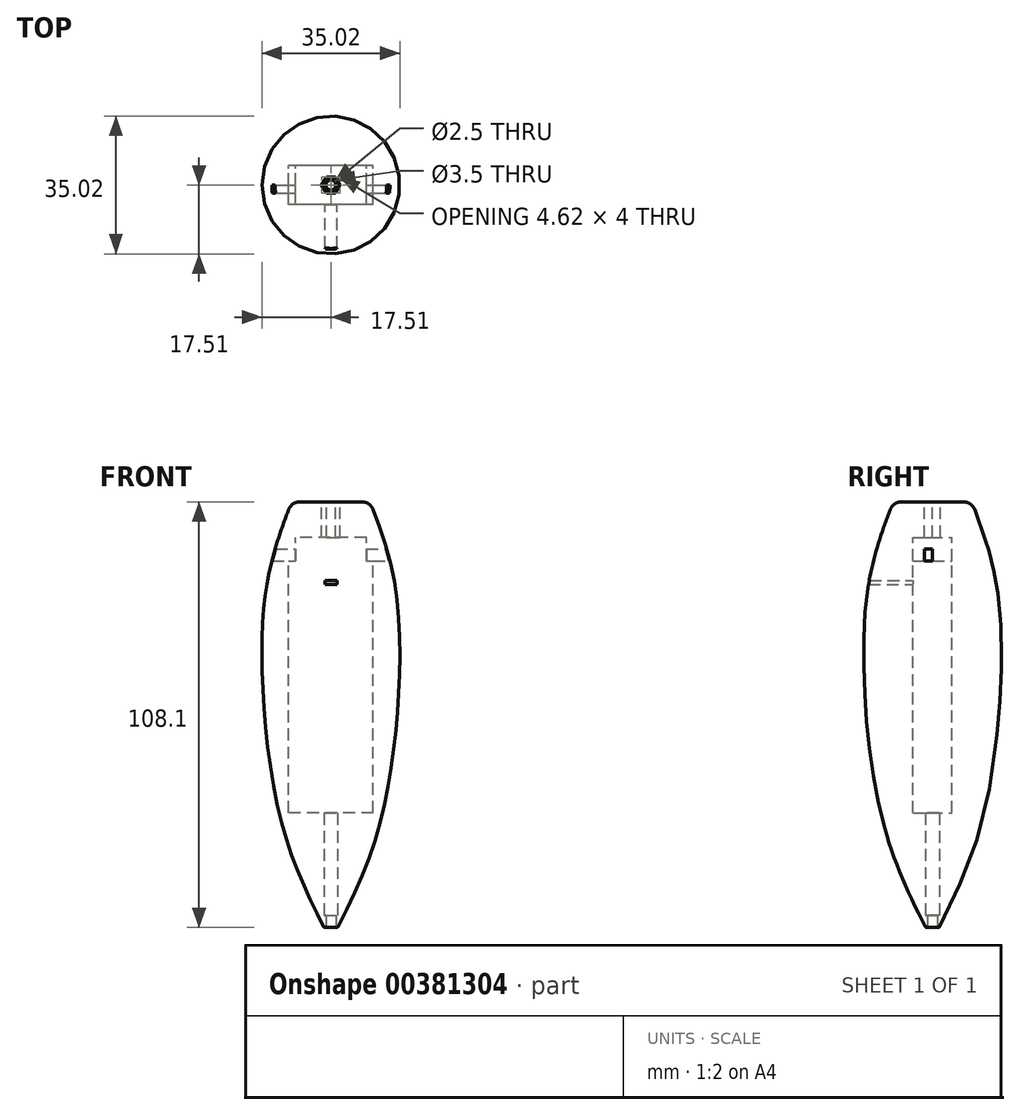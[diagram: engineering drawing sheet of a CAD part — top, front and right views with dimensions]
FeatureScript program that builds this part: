
annotation { "Feature Type Name" : "Feature", "Feature Type Description" : "" }
export const myFeature = defineFeature(function(context is Context, id is Id, definition is map)
    precondition{}
    {
        {
            var Q0;
            Q0=qCreatedBy(makeId("Front.planeOp"),FACE);
            var sketch = newSketch(context, id + "F0", { "sketchPlane" : qUnion([Q0])});
            skLineSegment(sketch, "E0.bottom", {"start": v(10.75, -17) * mm, "end": v(-10.75, -17) * mm});
            skLineSegment(sketch, "E0.top", {"start": v(10.75, 47) * mm, "end": v(9, 47) * mm});
            skLineSegment(sketch, "E0.left", {"start": v(10.75, -17) * mm, "end": v(10.75, 47) * mm});
            skLineSegment(sketch, "E0.right", {"start": v(-10.75, -17) * mm, "end": v(-10.75, 47) * mm});
            skPoint(sketch, "E0.middle", {"position": v(0, 15) * mm});
            skLineSegment(sketch, "E1", {"start": v(-10.75, 0) * mm, "end": v(10.75, 0) * mm, "construction": true});
            skLineSegment(sketch, "E2.top", {"start": v(9, 53) * mm, "end": v(-9, 53) * mm});
            skLineSegment(sketch, "E2.left", {"start": v(9, 47) * mm, "end": v(9, 53) * mm});
            skLineSegment(sketch, "E2.right", {"start": v(-9, 47) * mm, "end": v(-9, 53) * mm});
            skPoint(sketch, "E2.middle", {"position": v(0, 50) * mm});
            skPoint(sketch, "E2.middle.positionSnap0", {"position": v(0, 47) * mm});
            skPoint(sketch, "E2.centerSnap0", {"position": v(0, 47) * mm});
            skLineSegment(sketch, "E3.trimOffspring", {"start": v(-9, 47) * mm, "end": v(-10.75, 47) * mm});
            skSolve(sketch);
        }
        {
            var Q0;
            Q0=qCreatedBy(makeId("Front.planeOp"),FACE);
            var sketch = newSketch(context, id + "F1", { "sketchPlane" : qUnion([Q0])});
            skLineSegment(sketch, "E4", {"start": v(0, 0) * mm, "end": v(0, 25) * mm, "construction": true});
            skLineSegment(sketch, "E5", {"start": v(-17.5, 25) * mm, "end": v(17.5, 25) * mm, "construction": true});
            skLineSegment(sketch, "E6", {"start": v(-15, 47) * mm, "end": v(-2, 47) * mm, "construction": true});
            skPoint(sketch, "E7", {"position": v(0, 47) * mm});
            skPoint(sketch, "E8", {"position": v(0, -19.5) * mm});
            skLineSegment(sketch, "E9", {"start": v(-12.5, -19.5) * mm, "end": v(-1.25, -19.5) * mm, "construction": true});
            skLineSegment(sketch, "E10", {"start": v(0, -19.5) * mm, "end": v(0, -49.5) * mm, "construction": true});
            skLineSegment(sketch, "E11", {"start": v(0, 47) * mm, "end": v(0, 62) * mm, "construction": true});
            skLineSegment(sketch, "E12", {"start": v(-10, 62) * mm, "end": v(-2, 62) * mm});
            skFitSpline(sketch, "E13", {"points": [v(-10, 62) * mm, v(-15, 47) * mm, v(-17.5, 25) * mm, v(-12.5, -19.5) * mm, v(0, -49.5) * mm], "startDerivative": vector(-28.9, -76.62) * mm, "endDerivative": vector(51.56, -101.04) * mm});
            skLineSegment(sketch, "E14.0", {"start": v(-2, 50) * mm, "end": v(-2, 62) * mm});
            skPoint(sketch, "E15.orphan", {"position": v(10, 62) * mm});
            skLineSegment(sketch, "E16.0", {"start": v(-1.25, -43.05) * mm, "end": v(-1.25, -47.05) * mm});
            skLineSegment(sketch, "E17", {"start": v(0, 47) * mm, "end": v(-2, 47) * mm});
            skLineSegment(sketch, "E18", {"start": v(0, 50) * mm, "end": v(-2, 50) * mm});
            skLineSegment(sketch, "E19.trimOffspring", {"start": v(0, 47) * mm, "end": v(15, 47) * mm, "construction": true});
            skLineSegment(sketch, "E20.trimOffspring", {"start": v(0, -19.5) * mm, "end": v(12.5, -19.5) * mm, "construction": true});
            skLineSegment(sketch, "E21", {"start": v(0, 50) * mm, "end": v(0, -17) * mm});
            skLineSegment(sketch, "E22", {"start": v(0, -17) * mm, "end": v(-1.75, -17) * mm});
            skLineSegment(sketch, "E23", {"start": v(-1.75, -17) * mm, "end": v(-1.75, -43.05) * mm});
            skLineSegment(sketch, "E24", {"start": v(-1.25, -43.05) * mm, "end": v(-1.75, -43.05) * mm});
            skSolve(sketch);
        }
        {
            var Q0;
            Q0=makeQuery(id+"F1.imprint","IMPRINT",FACE,{"disambiguationData":[TD([[makeQuery(id+"F1.imprint","IMPRINT",EDGE,{"derivedFrom":sQuery(id+"F1.wireOp",EDGE,"E12")}),-1.0]])]});
            var Q1;
            Q1=sQuery(id+"F1.wireOp",EDGE,"E11");
            revolve(context, id + "F2", {"entities" : qUnion([Q0]), "axis" : qUnion([Q1]), "revolveType" : RevolveType.FULL});
        }
        {
            var Q0;
            Q0 = qSketchRegion(id + "F0", true);
            extrude(context, id + "F3", {"entities" : qUnion([Q0]), "operationType" : NewBodyOperationType.REMOVE, "endBound" : BoundingType.SYMMETRIC, "depth" : 10 * mm});
        }
        {
            var Q0;
            Q0=makeQuery(id+"F2.opRevolve","SWEPT_FACE",FACE,{"disambiguationData":[OSD([sQuery(id+"F1.wireOp",EDGE,"E12")])]});
            var sketch = newSketch(context, id + "F4", { "sketchPlane" : qUnion([Q0])});
            skCircle(sketch, "E25.cCircle", {"center": v(0, 0) * mm, "radius": 2 * mm, "construction": true});
            skLineSegment(sketch, "E25.0", {"start": v(2.3, 0) * mm, "end": v(1.15, -2) * mm});
            skLineSegment(sketch, "E25.1", {"start": v(1.15, -2) * mm, "end": v(-1.15, -2) * mm});
            skLineSegment(sketch, "E25.2", {"start": v(-1.15, -2) * mm, "end": v(-2.3, 0) * mm});
            skLineSegment(sketch, "E25.3", {"start": v(-2.3, 0) * mm, "end": v(-1.15, 2) * mm});
            skLineSegment(sketch, "E25.4", {"start": v(-1.15, 2) * mm, "end": v(1.15, 2) * mm});
            skLineSegment(sketch, "E25.5", {"start": v(1.15, 2) * mm, "end": v(2.3, 0) * mm});
            skPoint(sketch, "E25.0.midPoint", {"position": v(1.73, -1) * mm});
            skSolve(sketch);
        }
        {
            var Q0;
            Q0 = qSketchRegion(id + "F4", true);
            extrude(context, id + "F5", {"entities" : qUnion([Q0]), "operationType" : NewBodyOperationType.REMOVE, "oppositeDirection" : true, "depth" : 15 * mm});
        }
        {
            var Q0;
            Q0=qCreatedBy(makeId("Right.planeOp"),FACE);
            var sketch = newSketch(context, id + "F6", { "sketchPlane" : qUnion([Q0])});
            skLineSegment(sketch, "E26.bottom", {"start": v(0, 47) * mm, "end": v(-2, 47) * mm});
            skLineSegment(sketch, "E26.top", {"start": v(0, 50) * mm, "end": v(-2, 50) * mm});
            skLineSegment(sketch, "E26.left", {"start": v(0, 47) * mm, "end": v(0, 50) * mm});
            skLineSegment(sketch, "E26.right", {"start": v(-2, 47) * mm, "end": v(-2, 50) * mm});
            skPoint(sketch, "E26.middle", {"position": v(0, 48) * mm});
            skSolve(sketch);
        }
        {
            var Q0;
            Q0 = qSketchRegion(id + "F6", true);
            extrude(context, id + "F7", {"entities" : qUnion([Q0]), "operationType" : NewBodyOperationType.REMOVE, "endBound" : BoundingType.SYMMETRIC, "oppositeDirection" : true, "depth" : 41 * mm});
        }
        {
            var Q0;
            Q0=qCreatedBy(makeId("Front.planeOp"),FACE);
            var sketch = newSketch(context, id + "F8", { "sketchPlane" : qUnion([Q0])});
            skLineSegment(sketch, "E27.bottom", {"start": v(1.5, 41) * mm, "end": v(-1.5, 41) * mm});
            skLineSegment(sketch, "E27.top", {"start": v(1.5, 42) * mm, "end": v(-1.5, 42) * mm});
            skLineSegment(sketch, "E27.left", {"start": v(1.5, 41) * mm, "end": v(1.5, 42) * mm});
            skLineSegment(sketch, "E27.right", {"start": v(-1.5, 41) * mm, "end": v(-1.5, 42) * mm});
            skPoint(sketch, "E27.middle", {"position": v(0, 41.5) * mm});
            skSolve(sketch);
        }
        {
            var Q0;
            Q0 = qSketchRegion(id + "F8", true);
            extrude(context, id + "F9", {"entities" : qUnion([Q0]), "operationType" : NewBodyOperationType.REMOVE, "endBound" : BoundingType.THROUGH_ALL, "depth" : 25 * mm});
        }
        {
            var Q0;
            Q0=makeQuery(id+"F2.opRevolve","SWEPT_EDGE",EDGE,{"disambiguationData":[OSD([sQuery(id+"F1.wireOp",EDGE,"E13"),sQuery(id+"F1.wireOp",EDGE,"E16.0")])]});
            fillet(context, id + "F10", {"entities" : qUnion([Q0]), "radius" : 0.3 * mm, "tangentPropagation" : true, "allowEdgeOverflow" : false});
        }
        {
            var Q0;
            Q0=makeQuery(id+"F2.opRevolve","SWEPT_EDGE",EDGE,{"disambiguationData":[OSD([sQuery(id+"F1.wireOp",EDGE,"E16.0"),sQuery(id+"F1.wireOp",EDGE,"E24")])]});
            fillet(context, id + "F11", {"entities" : qUnion([Q0]), "radius" : 0.1 * mm, "tangentPropagation" : true, "allowEdgeOverflow" : false});
        }
        {
            var Q0;
            Q0=makeQuery(id+"F2.opRevolve","SWEPT_EDGE",EDGE,{"disambiguationData":[OSD([sQuery(id+"F1.wireOp",EDGE,"E23"),sQuery(id+"F1.wireOp",EDGE,"E24")])]});
            fillet(context, id + "F12", {"entities" : qUnion([Q0]), "radius" : 0.1 * mm, "tangentPropagation" : true, "allowEdgeOverflow" : false});
        }
        {
            var Q0;
            Q0=makeQuery(id+"F2.opRevolve","SWEPT_EDGE",EDGE,{"disambiguationData":[OSD([sQuery(id+"F1.wireOp",EDGE,"E12"),sQuery(id+"F1.wireOp",EDGE,"E13")])]});
            fillet(context, id + "F13", {"entities" : qUnion([Q0]), "radius" : 3 * mm, "tangentPropagation" : true, "allowEdgeOverflow" : false});
        }
    });
